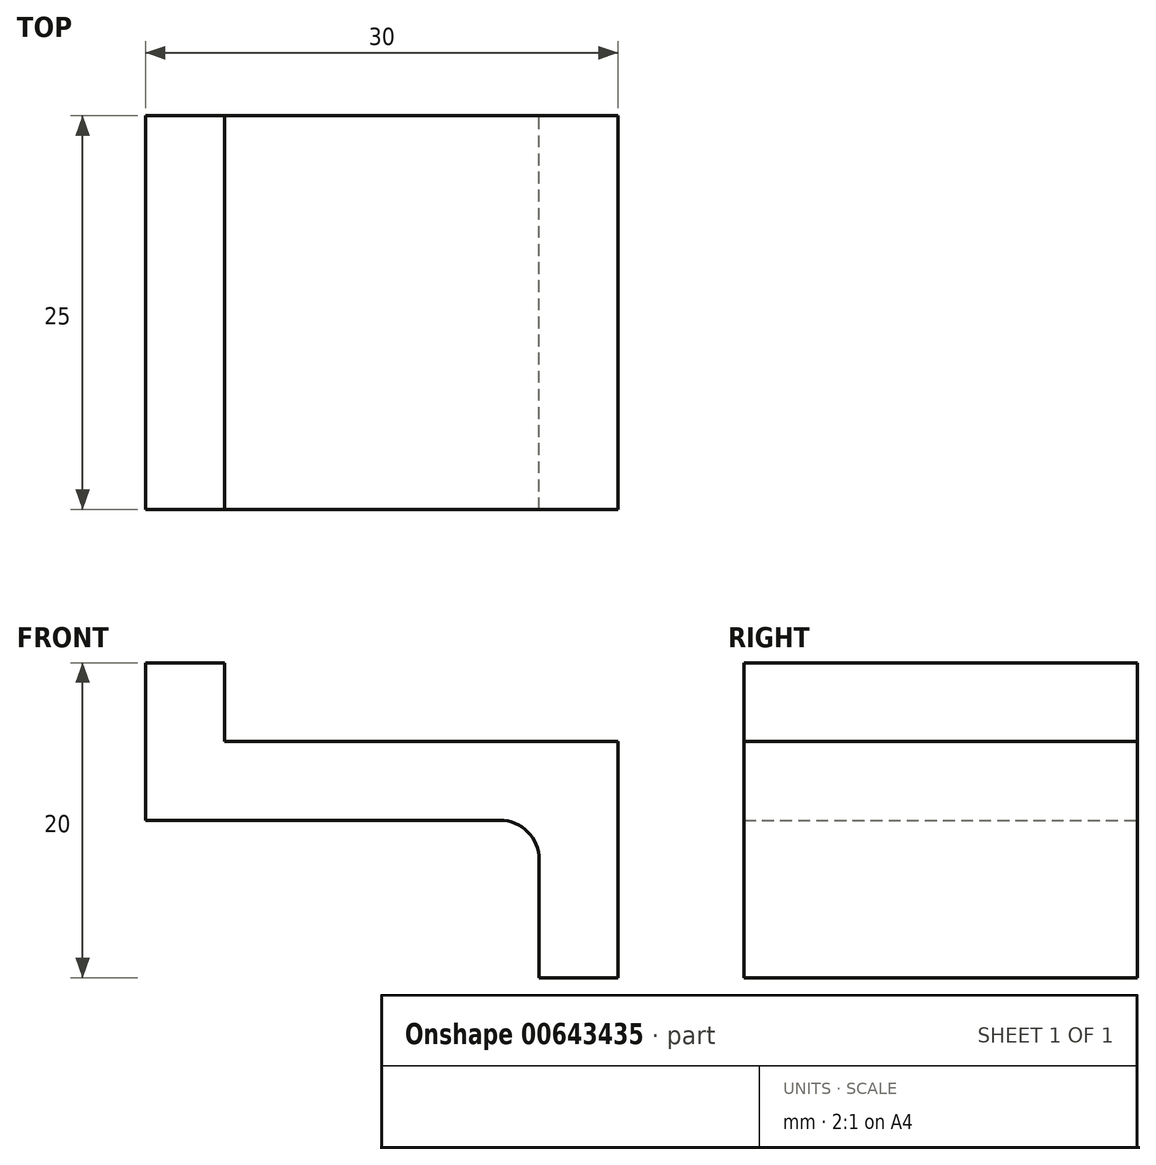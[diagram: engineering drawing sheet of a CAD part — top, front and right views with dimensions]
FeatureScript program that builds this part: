
annotation { "Feature Type Name" : "Feature", "Feature Type Description" : "" }
export const myFeature = defineFeature(function(context is Context, id is Id, definition is map)
    precondition{}
    {
        {
            var Q0;
            Q0=qCreatedBy(makeId("Front.planeOp"),FACE);
            var sketch = newSketch(context, id + "F0", { "sketchPlane" : qUnion([Q0])});
            skLineSegment(sketch, "E0", {"start": v(0, 0) * mm, "end": v(-2.63, 0) * mm});
            skLineSegment(sketch, "E1", {"start": v(-25, 0) * mm, "end": v(-2.5, 0) * mm});
            skLineSegment(sketch, "E2", {"start": v(-25, 0) * mm, "end": v(-25, 10) * mm});
            skLineSegment(sketch, "E3", {"start": v(-25, 10) * mm, "end": v(-20, 10) * mm});
            skLineSegment(sketch, "E4", {"start": v(-20, 10) * mm, "end": v(-20, 5) * mm});
            skLineSegment(sketch, "E5", {"start": v(-20, 5) * mm, "end": v(5, 5) * mm});
            skLineSegment(sketch, "E6", {"start": v(5, 5) * mm, "end": v(5, -10) * mm});
            skLineSegment(sketch, "E7", {"start": v(5, -10) * mm, "end": v(0, -10) * mm});
            skLineSegment(sketch, "E8", {"start": v(0, -10) * mm, "end": v(0, -2.5) * mm});
            skPoint(sketch, "E9.visualSharp", {"position": v(0, 0) * mm});
            skArc(sketch, "E9.filletArc", {"start": v(0, -2.5) * mm, "mid": v(-0.73, -0.73) * mm, "end": v(-2.5, 0) * mm});
            skSolve(sketch);
        }
        {
            var Q0;
            Q0 = qSketchRegion(id + "F0", true);
            extrude(context, id + "F1", {"entities" : qUnion([Q0]), "depth" : 25 * mm, "offsetDistance" : 25 * mm});
        }
    });
